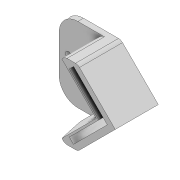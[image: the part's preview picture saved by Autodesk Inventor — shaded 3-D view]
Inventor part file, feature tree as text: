
AUTODESK INVENTOR PART (.ipt)
format: ipt  version: 2022 (Build 260153000, 153)  size: 165,888 bytes
history: native  units: mm
features: extrude x2, chamfer x2, fillet x2, sketch x2, other x1
ambient origin geometry x8: Origin, YZ Plane, XZ Plane, XY Plane, X Axis, Y Axis, Z Axis, Center Point
bodies: Body1 (feature_tree)
feature tree (9):
  other  "Sólido1"
  extrude  "Extrusión1"  Depth=40.0mm
  extrude  "Extrusión2"  TaperAngle=0.0deg  [1 undecoded]
  chamfer  "Chaflán1"  Distance=3.2mm
  chamfer  "Chaflán2"  Distance=3.2mm
  fillet  "Empalme1"  Radius=20.0mm
  fillet  "Empalme2"  Radius=10.0mm
  sketch  "Boceto1"  dims[d0=30.0mm d1=40.0mm]
  sketch  "Boceto2"  dims[d2=90.0deg d3=0.0mm d4=3.2mm d5=3.2mm d6=20.0mm d7=10.0mm d8=2.0mm d9=8.0mm d10=3.0mm d11=0.0mm d12=3.0mm d13=3.2mm d14=3.0mm d15=25.5mm d16=25.5mm d17=180.0deg d18=180.0deg d19=3.0mm d20=3.0mm d21=3.0mm d22=3.2mm d23=20.0mm d24=0.0mm d25=2.0mm d26=10.0mm d27=45.0deg d28=2.0mm d29=10.0mm d30=45.0deg d31=3.0mm d32=10.0mm]
note: 1 required parameter value undecoded (feature->parameter linkage not recoverable at this tier; creation-order binding heuristic only, values carry confidence <= 0.55)
